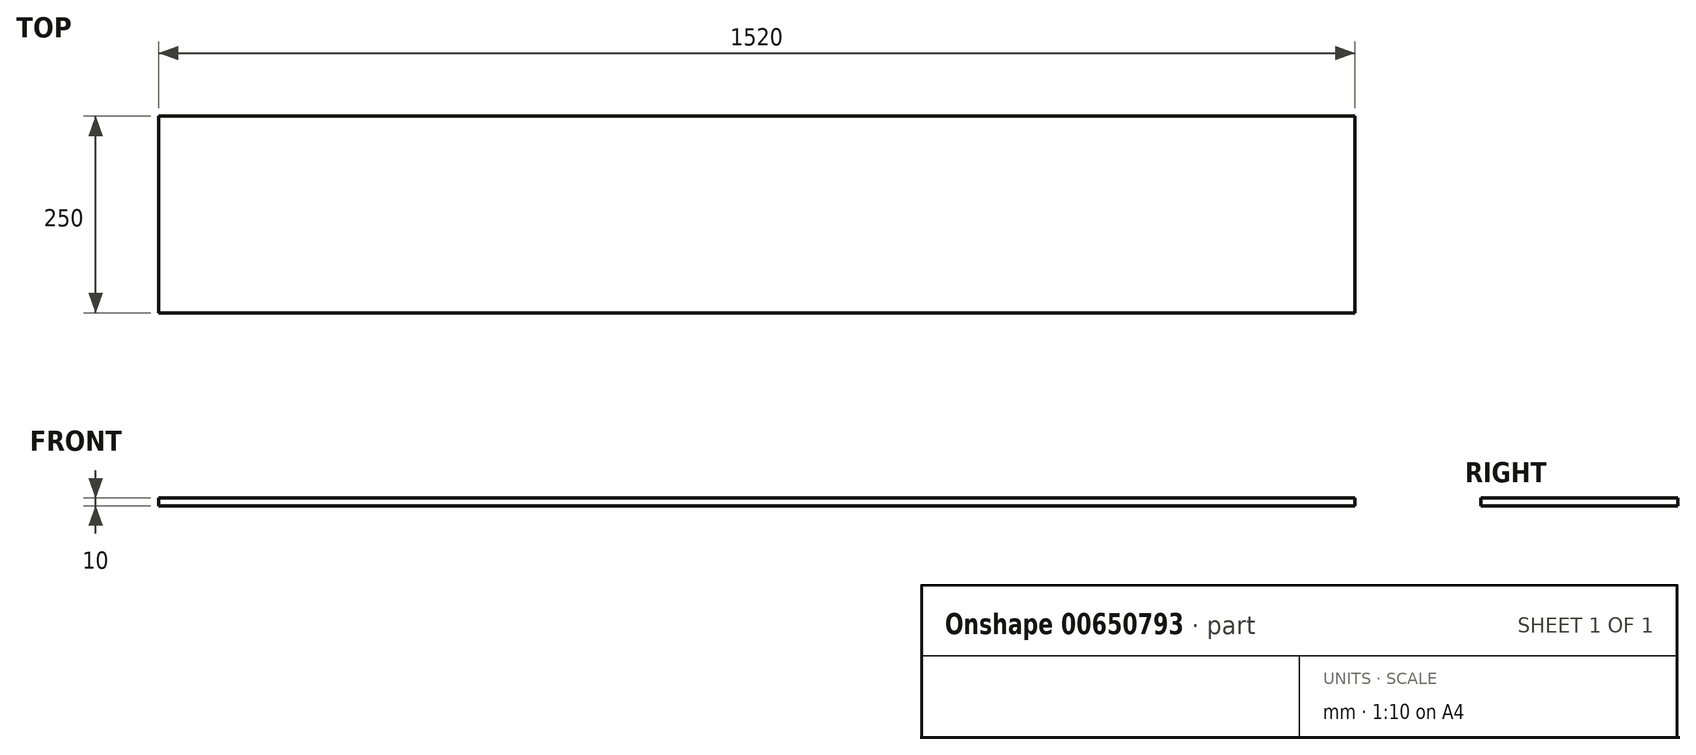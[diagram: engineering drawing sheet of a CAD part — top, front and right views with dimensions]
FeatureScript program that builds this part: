
annotation { "Feature Type Name" : "Feature", "Feature Type Description" : "" }
export const myFeature = defineFeature(function(context is Context, id is Id, definition is map)
    precondition{}
    {
        {
            var Q0;
            Q0=qCreatedBy(makeId("Top.planeOp"),FACE);
            var sketch = newSketch(context, id + "F0", { "sketchPlane" : qUnion([Q0])});
            skLineSegment(sketch, "E0.bottom", {"start": v(-2067.28, 0) * mm, "end": v(-547.28, 0) * mm});
            skLineSegment(sketch, "E0.top", {"start": v(-2067.28, -250) * mm, "end": v(-547.28, -250) * mm});
            skLineSegment(sketch, "E0.left", {"start": v(-2067.28, 0) * mm, "end": v(-2067.28, -250) * mm});
            skLineSegment(sketch, "E0.right", {"start": v(-547.28, 0) * mm, "end": v(-547.28, -250) * mm});
            skSolve(sketch);
        }
        {
            var Q0;
            Q0=makeQuery(id+"F0.imprint","IMPRINT",FACE,{"disambiguationData":[TD([[makeQuery(id+"F0.imprint","IMPRINT",EDGE,{"derivedFrom":sQuery(id+"F0.wireOp",EDGE,"E0.bottom")}),-1.0]])]});
            extrude(context, id + "F1", {"entities" : qUnion([Q0]), "depth" : 10 * mm, "offsetDistance" : 25 * mm});
        }
    });
